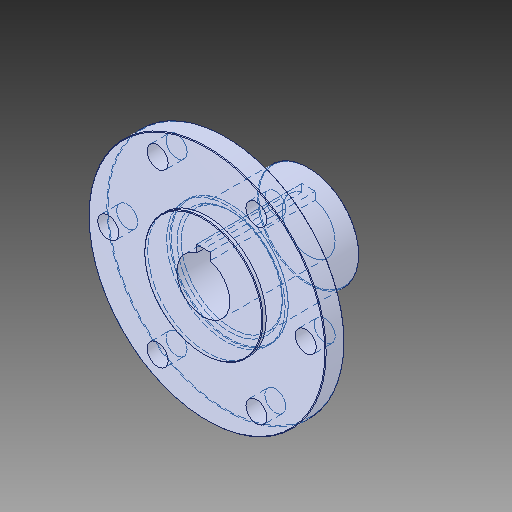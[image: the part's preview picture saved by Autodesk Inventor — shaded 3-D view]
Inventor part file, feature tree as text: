
AUTODESK INVENTOR PART (.ipt)
format: ipt  version: 2019 (Build 230136000, 136)  size: 161,280 bytes
history: native  units: in
note: dims shown in document units (in); Inventor stores cm internally (conversion verified against a paired STEP export)
features: chamfer x1
ambient origin geometry x8: Origin, YZ Plane, XZ Plane, XY Plane, X Axis, Y Axis, Z Axis, Center Point
bodies: Solid1 (feature_tree)
feature tree (1):
  chamfer  "Chamfer2"  [1 undecoded]
note: 1 required parameter value undecoded (feature->parameter linkage not recoverable at this tier; creation-order binding heuristic only, values carry confidence <= 0.55)
